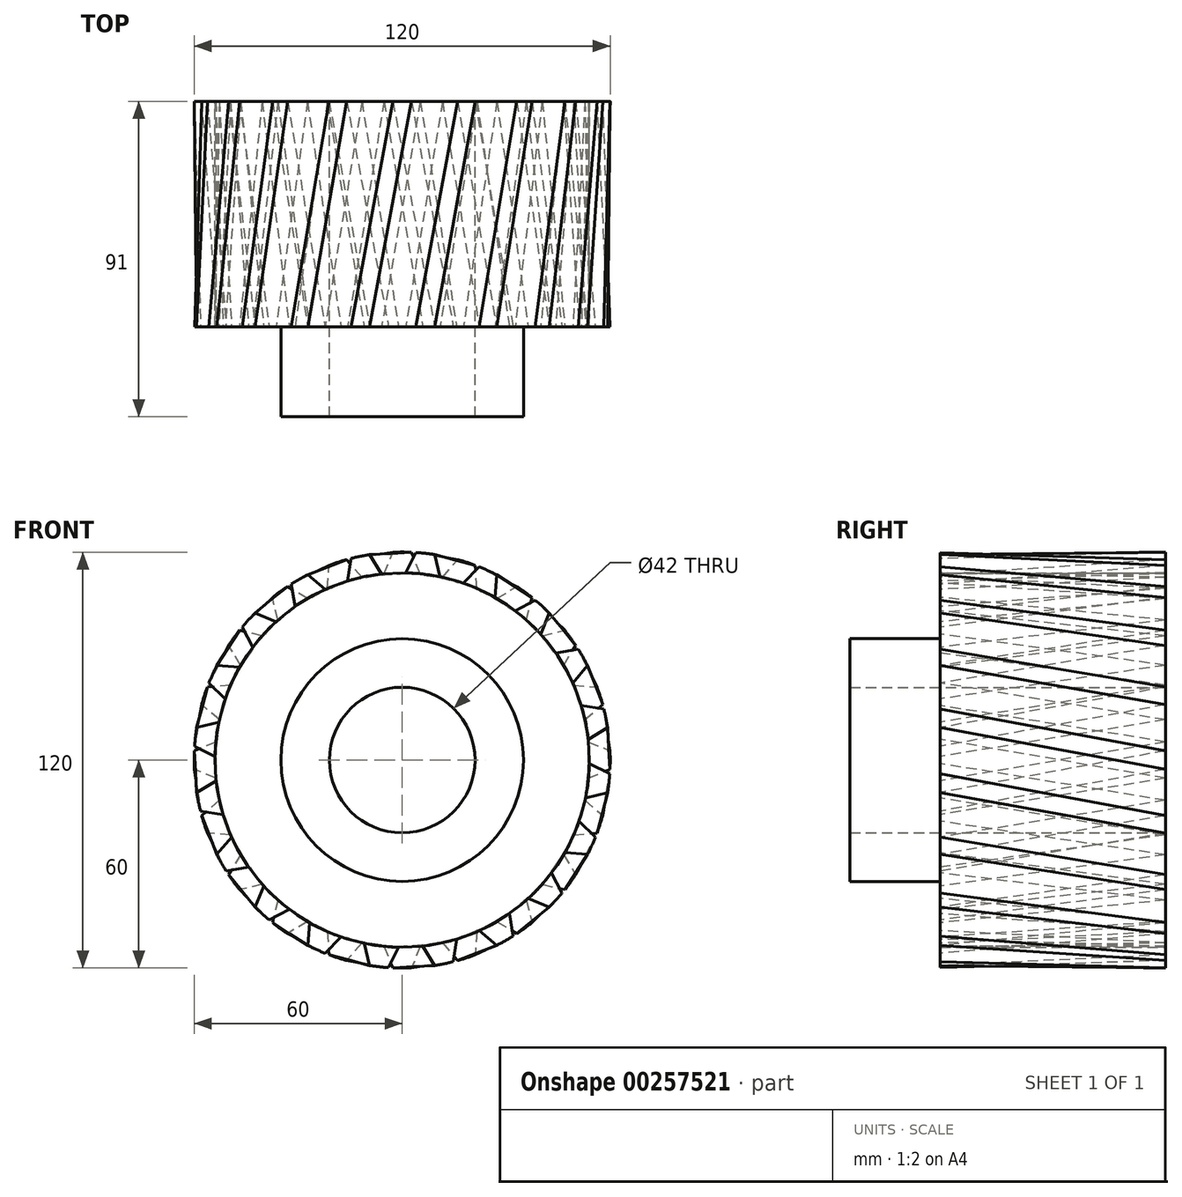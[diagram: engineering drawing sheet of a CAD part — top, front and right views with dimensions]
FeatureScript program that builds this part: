
annotation { "Feature Type Name" : "Feature", "Feature Type Description" : "" }
export const myFeature = defineFeature(function(context is Context, id is Id, definition is map)
    precondition{}
    {
        {
            var Q0;
            Q0=qCreatedBy(makeId("Front.planeOp"),FACE);
            var sketch = newSketch(context, id + "F0", { "sketchPlane" : qUnion([Q0])});
            skCircle(sketch, "E0", {"center": v(0, 0) * mm, "radius": 54 * mm});
            skCircle(sketch, "E1", {"center": v(0, 0) * mm, "radius": 21 * mm});
            skSolve(sketch);
        }
        {
            var Q0;
            Q0=makeQuery(id+"F0.imprint","IMPRINT",FACE,{"disambiguationData":[TD([[makeQuery(id+"F0.imprint","IMPRINT",EDGE,{"derivedFrom":sQuery(id+"F0.wireOp",EDGE,"E0")}),1.0]])]});
            extrude(context, id + "F1", {"entities" : qUnion([Q0]), "depth" : 65 * mm});
        }
        {
            var Q0;
            Q0=makeQuery(id+"F1.opExtrude","CAP_FACE",FACE,{"disambiguationData":[OSD([sQuery(id+"F0.wireOp",EDGE,"E0")])],"isStart":false});
            var sketch = newSketch(context, id + "F2", { "sketchPlane" : qUnion([Q0])});
            skPoint(sketch, "E2.0", {"position": v(0, 0) * mm});
            skCircle(sketch, "E3", {"center": v(0, 0) * mm, "radius": 35 * mm});
            skCircle(sketch, "E4", {"center": v(0, 0) * mm, "radius": 21 * mm});
            skSolve(sketch);
        }
        {
            var Q0;
            Q0=makeQuery(id+"F2.imprint","IMPRINT",FACE,{"disambiguationData":[TD([[makeQuery(id+"F2.imprint","IMPRINT",EDGE,{"derivedFrom":sQuery(id+"F2.wireOp",EDGE,"E3")}),1.0]])]});
            extrude(context, id + "F3", {"entities" : qUnion([Q0]), "operationType" : NewBodyOperationType.ADD, "depth" : 26 * mm});
        }
        {
            var Q0;
            Q0=qCreatedBy(makeId("Right.planeOp"),FACE);
            cPlane(context, id + "F4", {"entities" : qUnion([Q0]), "cplaneType" : CPlaneType.OFFSET, "offset" : 60 * mm, "width" : 150 * mm, "height" : 150 * mm});
        }
        {
            var Q0;
            Q0=qCreatedBy(id+"F4.planeOp",FACE);
            var sketch = newSketch(context, id + "F5", { "sketchPlane" : qUnion([Q0])});
            skLineSegment(sketch, "E5.0", {"start": v(-65, -54) * mm, "end": v(-65, 54) * mm});
            skLineSegment(sketch, "E6.0", {"start": v(0, -54) * mm, "end": v(0, 54) * mm});
            skLineSegment(sketch, "E7", {"start": v(0, -3.11) * mm, "end": v(-65, -30.54) * mm});
            skLineSegment(sketch, "E8", {"start": v(0, 3.11) * mm, "end": v(-65, -24.31) * mm});
            skLineSegment(sketch, "E9", {"start": v(0, 3.11) * mm, "end": v(0, -3.11) * mm});
            skLineSegment(sketch, "E10", {"start": v(-65, -24.31) * mm, "end": v(-65, -30.54) * mm});
            skSolve(sketch);
        }
        {
            var Q0;
            Q0=qCreatedBy(makeId("Right.planeOp"),FACE);
            var sketch = newSketch(context, id + "F6", { "sketchPlane" : qUnion([Q0])});
            skLineSegment(sketch, "E11", {"start": v(32.15, 0) * mm, "end": v(-118.2, 0) * mm, "construction": true});
            skSolve(sketch);
        }
        {
            var Q0;
            Q0=qCreatedBy(makeId("Front.planeOp"),FACE);
            var sketch = newSketch(context, id + "F7", { "sketchPlane" : qUnion([Q0])});
            skCircle(sketch, "E12", {"center": v(0, 0) * mm, "radius": 60 * mm});
            skCircle(sketch, "E13.0", {"center": v(0, 0) * mm, "radius": 54 * mm});
            skLineSegment(sketch, "E14", {"start": v(0, 0) * mm, "end": v(88.72, 0) * mm, "construction": true});
            skLineSegment(sketch, "E15", {"start": v(53.74, -5.25) * mm, "end": v(59.94, -2.68) * mm});
            skLineSegment(sketch, "E16.MirrorCS", {"start": v(53.74, 5.25) * mm, "end": v(59.94, 2.68) * mm});
            skSolve(sketch);
        }
        {
            var Q0;
            Q0=qCreatedBy(makeId("Right.planeOp"),FACE);
            var Q1;
            Q1=sQuery(id+"F7.wireOp",VERTEX,"E16.MirrorCS.end");
            cPlane(context, id + "F8", {"entities" : qUnion([Q0, Q1]), "cplaneType" : CPlaneType.PLANE_POINT, "offset" : 25 * mm, "width" : 150 * mm, "height" : 150 * mm});
        }
        {
            var Q0;
            Q0=qCreatedBy(id+"F8.planeOp",FACE);
            var sketch = newSketch(context, id + "F9", { "sketchPlane" : qUnion([Q0])});
            skPoint(sketch, "E17.0", {"position": v(0, 2.68) * mm});
            skLineSegment(sketch, "E18.0", {"start": v(-65, -54) * mm, "end": v(-65, 54) * mm});
            skLineSegment(sketch, "E19", {"start": v(0, 2.68) * mm, "end": v(-65, 14.76) * mm});
            skPoint(sketch, "E20.0", {"position": v(0, -2.68) * mm});
            skLineSegment(sketch, "E21.0.0", {"start": v(0, 54) * mm, "end": v(0, -54) * mm});
            skLineSegment(sketch, "E21.0.1", {"start": v(0, 5.25) * mm, "end": v(0, 2.68) * mm});
            skLineSegment(sketch, "E21.0.2", {"start": v(0, -60) * mm, "end": v(0, 60) * mm});
            skLineSegment(sketch, "E21.0.3", {"start": v(0, -2.68) * mm, "end": v(0, -5.25) * mm});
            skLineSegment(sketch, "E22", {"start": v(0, -2.68) * mm, "end": v(-65, 9.39) * mm});
            skSolve(sketch);
        }
        {
            var Q0;
            Q0=makeQuery(id+"F1.opExtrude","CAP_FACE",FACE,{"disambiguationData":[OSD([sQuery(id+"F0.wireOp",EDGE,"E0"),sQuery(id+"F0.wireOp",EDGE,"E1")])],"isStart":false});
            var sketch = newSketch(context, id + "F10", { "sketchPlane" : qUnion([Q0])});
            skPoint(sketch, "E23.0", {"position": v(59.94, 9.39) * mm});
            skPoint(sketch, "E24.0", {"position": v(59.94, 14.76) * mm});
            skCircle(sketch, "E25.0", {"center": v(0, 0) * mm, "radius": 60 * mm});
            skLineSegment(sketch, "E26", {"start": v(59.26, 9.39) * mm, "end": v(58.16, 14.76) * mm, "construction": true});
            skPoint(sketch, "E27", {"position": v(58.7, 12.07) * mm});
            skLineSegment(sketch, "E28", {"start": v(58.7, 12.07) * mm, "end": v(50.9, 10.47) * mm, "construction": true});
            skLineSegment(sketch, "E29", {"start": v(59.26, 9.39) * mm, "end": v(53.67, 5.95) * mm});
            skLineSegment(sketch, "E30.MirrorCS", {"start": v(58.16, 14.76) * mm, "end": v(51.66, 15.71) * mm});
            skLineSegment(sketch, "E31", {"start": v(58.16, 14.76) * mm, "end": v(53.55, 13.8) * mm});
            skSolve(sketch);
        }
        {
            var Q1;
            {var subQ0=sQuery(id+"F7.wireOp",EDGE,"E15");Q1=makeQuery(id+"F7.imprint","IMPRINT",FACE,{"disambiguationData":[TD([[makeQuery(id+"F7.imprint","IMPRINT",EDGE,{"derivedFrom":subQ0}),1.0]])]});}
            var Q2;
            {var subQ0=sQuery(id+"F10.wireOp",EDGE,"E29");Q2=makeQuery(id+"F10.imprint","IMPRINT",FACE,{"disambiguationData":[TD([[makeQuery(id+"F10.imprint","IMPRINT",EDGE,{"derivedFrom":subQ0}),-1.0]])]});}
            loft(context, id + "F11", {"sheetProfilesArray" : [{ "sheetProfileEntities" : qUnion([Q1]) }, { "sheetProfileEntities" : qUnion([Q2]) }]});
        }
        {
            var Q0;
            {var subQ0=sQuery(id+"F10.wireOp",EDGE,"E29");var subQ4=sQuery(id+"F7.wireOp",EDGE,"E15");Q0=makeQuery(id+"F11.opLoft","SWEPT_BODY",BODY,{"disambiguationData":[OSD([makeQuery(id+"F7.imprint","IMPRINT",FACE,{"disambiguationData":[TD([[makeQuery(id+"F7.imprint","IMPRINT",EDGE,{"derivedFrom":subQ4}),1.0]])]}),makeQuery(id+"F10.imprint","IMPRINT",FACE,{"disambiguationData":[TD([[makeQuery(id+"F10.imprint","IMPRINT",EDGE,{"derivedFrom":subQ0}),-1.0]])]})])]});}
            var Q1;
            Q1=sQuery(id+"F6.wireOp",EDGE,"E11");
            circularPattern(context, id + "F12", {"entities" : qUnion([Q0]), "axis" : qUnion([Q1]), "angle" : 360 * degree, "instanceCount" : 20, "equalSpace" : true});
        }
    });
